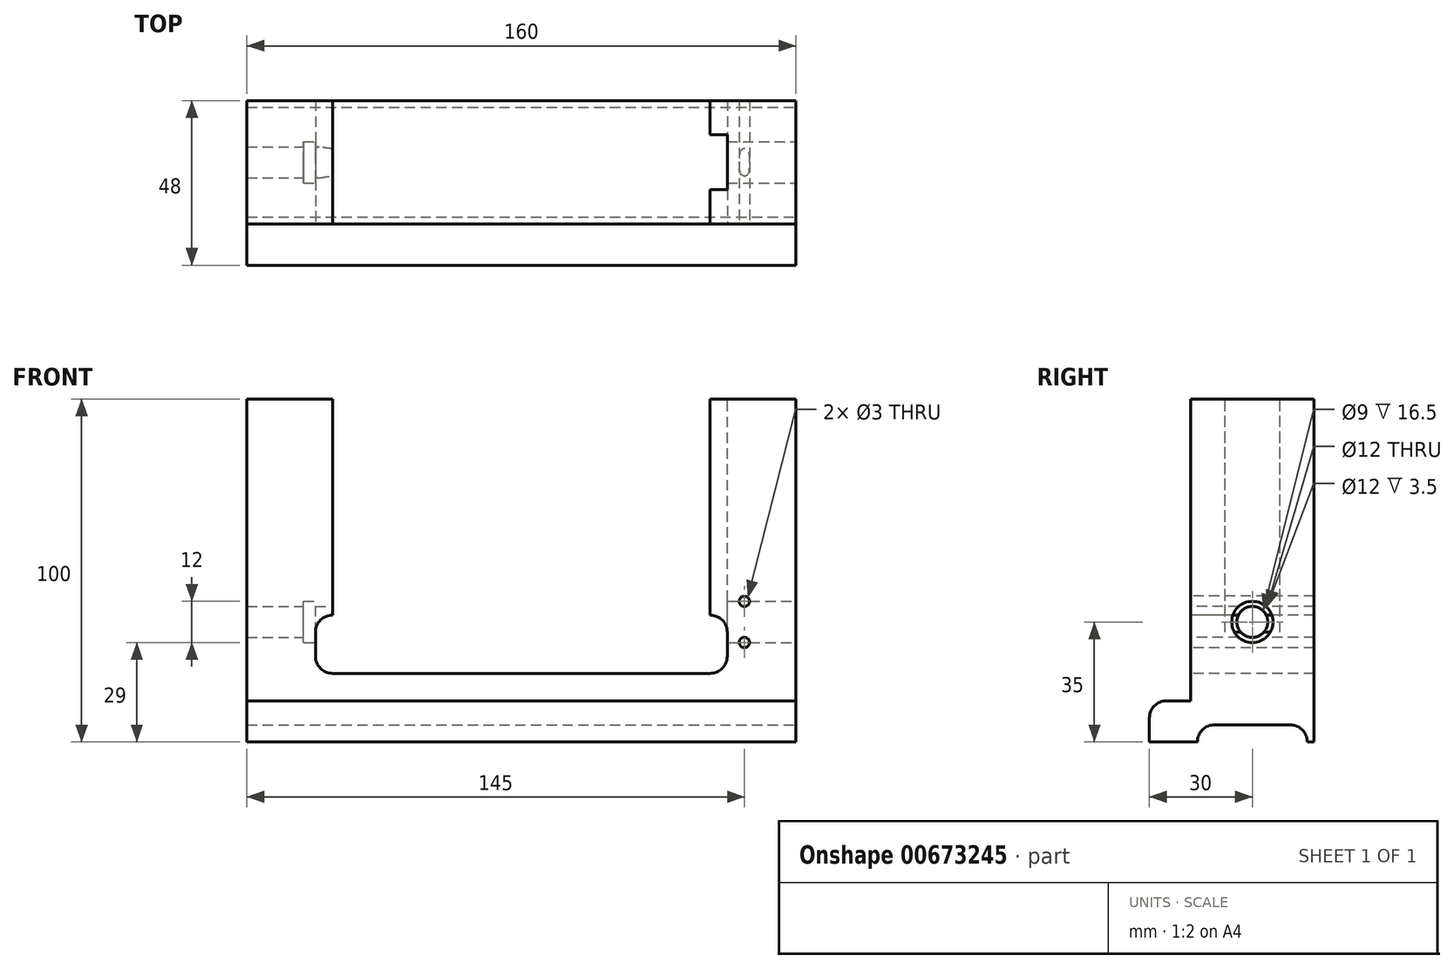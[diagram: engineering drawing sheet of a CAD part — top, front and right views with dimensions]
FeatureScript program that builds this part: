
annotation { "Feature Type Name" : "Feature", "Feature Type Description" : "" }
export const myFeature = defineFeature(function(context is Context, id is Id, definition is map)
    precondition{}
    {
        {
            var Q0;
            Q0=qCreatedBy(makeId("Front.planeOp"),FACE);
            var sketch = newSketch(context, id + "F0", { "sketchPlane" : qUnion([Q0])});
            skLineSegment(sketch, "E0.bottom", {"start": v(-80, 0) * mm, "end": v(80, 0) * mm});
            skLineSegment(sketch, "E0.top", {"start": v(-80, 100) * mm, "end": v(80, 100) * mm});
            skLineSegment(sketch, "E0.left", {"start": v(-80, 0) * mm, "end": v(-80, 100) * mm});
            skLineSegment(sketch, "E0.right", {"start": v(80, 0) * mm, "end": v(80, 100) * mm});
            skSolve(sketch);
        }
        {
            var Q0;
            Q0=makeQuery(id+"F0.imprint","IMPRINT",FACE,{"disambiguationData":[TD([[makeQuery(id+"F0.imprint","IMPRINT",EDGE,{"derivedFrom":sQuery(id+"F0.wireOp",EDGE,"E0.bottom")}),1.0]])]});
            extrude(context, id + "F1", {"entities" : qUnion([Q0]), "depth" : 36 * mm, "offsetDistance" : 25 * mm, "symmetric" : true});
        }
        {
            var Q0;
            Q0=makeQuery(id+"F1.opExtrude","CAP_FACE",FACE,{"disambiguationData":[OSD([sQuery(id+"F0.wireOp",EDGE,"E0.bottom"),sQuery(id+"F0.wireOp",EDGE,"E0.top"),sQuery(id+"F0.wireOp",EDGE,"E0.left"),sQuery(id+"F0.wireOp",EDGE,"E0.right")])],"isStart":false});
            var sketch = newSketch(context, id + "F2", { "sketchPlane" : qUnion([Q0])});
            skLineSegment(sketch, "E1.bottom", {"start": v(-80, 0) * mm, "end": v(80, 0) * mm});
            skLineSegment(sketch, "E1.top", {"start": v(-80, 12) * mm, "end": v(80, 12) * mm});
            skLineSegment(sketch, "E1.left", {"start": v(-80, 0) * mm, "end": v(-80, 12) * mm});
            skLineSegment(sketch, "E1.right", {"start": v(80, 0) * mm, "end": v(80, 12) * mm});
            skSolve(sketch);
        }
        {
            var Q0;
            Q0=makeQuery(id+"F2.imprint","IMPRINT",FACE,{"disambiguationData":[TD([[makeQuery(id+"F2.imprint","IMPRINT",EDGE,{"derivedFrom":sQuery(id+"F2.wireOp",EDGE,"E1.bottom")}),1.0]])]});
            extrude(context, id + "F3", {"entities" : qUnion([Q0]), "operationType" : NewBodyOperationType.ADD, "depth" : 12 * mm, "offsetDistance" : 25 * mm});
        }
        {
            var Q0;
            Q0=makeQuery(id+"F1.opExtrude","CAP_FACE",FACE,{"disambiguationData":[OSD([sQuery(id+"F0.wireOp",EDGE,"E0.bottom"),sQuery(id+"F0.wireOp",EDGE,"E0.top"),sQuery(id+"F0.wireOp",EDGE,"E0.left"),sQuery(id+"F0.wireOp",EDGE,"E0.right")])],"isStart":false});
            var sketch = newSketch(context, id + "F4", { "sketchPlane" : qUnion([Q0])});
            skLineSegment(sketch, "E2.bottom", {"start": v(-55, 100) * mm, "end": v(55, 100) * mm});
            skLineSegment(sketch, "E2.left", {"start": v(-55, 100) * mm, "end": v(-55, 37) * mm});
            skLineSegment(sketch, "E2.right", {"start": v(55, 100) * mm, "end": v(55, 37) * mm});
            skLineSegment(sketch, "E3.bottom", {"start": v(-60, 20) * mm, "end": v(60, 20) * mm});
            skLineSegment(sketch, "E3.top", {"start": v(-60, 37) * mm, "end": v(-55, 37) * mm});
            skLineSegment(sketch, "E3.left", {"start": v(-60, 20) * mm, "end": v(-60, 37) * mm});
            skLineSegment(sketch, "E3.right", {"start": v(60, 20) * mm, "end": v(60, 37) * mm});
            skLineSegment(sketch, "E4.trimOffspring", {"start": v(55, 37) * mm, "end": v(60, 37) * mm});
            skSolve(sketch);
        }
        {
            var Q0;
            Q0=makeQuery(id+"F4.imprint","IMPRINT",FACE,{"disambiguationData":[TD([[makeQuery(id+"F4.imprint","IMPRINT",EDGE,{"derivedFrom":sQuery(id+"F4.wireOp",EDGE,"E2.bottom")}),-1.0]])]});
            extrude(context, id + "F5", {"entities" : qUnion([Q0]), "operationType" : NewBodyOperationType.REMOVE, "endBound" : BoundingType.THROUGH_ALL, "oppositeDirection" : true, "depth" : 25 * mm, "offsetDistance" : 25 * mm});
        }
        {
            var Q0;
            Q0=makeQuery(id+"F3.opExtrude","CAP_EDGE",EDGE,{"disambiguationData":[OSD([sQuery(id+"F2.wireOp",EDGE,"E1.top")])],"isStart":true});
            var Q1;
            Q1=makeQuery(id+"F3.opExtrude","CAP_EDGE",EDGE,{"disambiguationData":[OSD([sQuery(id+"F2.wireOp",EDGE,"E1.top")])],"isStart":false});
            var Q2;
            Q2=makeQuery(id+"FdwUagCk7FOIXWf_1.1.F3.opExtrude","CAP_EDGE",EDGE,{"disambiguationData":[OSD([sQuery(id+"F2.wireOp",EDGE,"E1.top")])],"isStart":true});
            var Q3;
            Q3=makeQuery(id+"FdwUagCk7FOIXWf_1.1.F3.opExtrude","CAP_EDGE",EDGE,{"disambiguationData":[OSD([sQuery(id+"F2.wireOp",EDGE,"E1.top")])],"isStart":false});
            var Q4;
            Q4=makeQuery(id+"F5.boolean.opBoolean","COPY",EDGE,{"derivedFrom":makeQuery(id+"F5.opExtrude","SWEPT_EDGE",EDGE,{"disambiguationData":[OSD([sQuery(id+"F4.wireOp",EDGE,"E3.top"),sQuery(id+"F4.wireOp",EDGE,"E3.left")])]})});
            var Q5;
            Q5=makeQuery(id+"F5.boolean.opBoolean","COPY",EDGE,{"derivedFrom":makeQuery(id+"F5.opExtrude","SWEPT_EDGE",EDGE,{"disambiguationData":[OSD([sQuery(id+"F4.wireOp",EDGE,"E3.bottom"),sQuery(id+"F4.wireOp",EDGE,"E3.left")])]})});
            var Q6;
            Q6=makeQuery(id+"F5.boolean.opBoolean","COPY",EDGE,{"derivedFrom":makeQuery(id+"F5.opExtrude","SWEPT_EDGE",EDGE,{"disambiguationData":[OSD([sQuery(id+"F4.wireOp",EDGE,"E3.bottom"),sQuery(id+"F4.wireOp",EDGE,"E3.right")])]})});
            var Q7;
            Q7=makeQuery(id+"F5.boolean.opBoolean","COPY",EDGE,{"derivedFrom":makeQuery(id+"F5.opExtrude","SWEPT_EDGE",EDGE,{"disambiguationData":[OSD([sQuery(id+"F4.wireOp",EDGE,"E3.right"),sQuery(id+"F4.wireOp",EDGE,"E4.trimOffspring")])]})});
            fillet(context, id + "F6", {"entities" : qUnion([Q0, Q1, Q2, Q3, Q4, Q5, Q6, Q7]), "radius" : 5 * mm, "tangentPropagation" : true, "allowEdgeOverflow" : false});
        }
        {
            var Q0;
            {var subQ0=sQuery(id+"F2.wireOp",EDGE,"E1.right");Q0=makeQuery(id+"FdwUagCk7FOIXWf_1.1.F3.boolean.opBoolean","MERGE",FACE,{"derivedFrom":[makeQuery(id+"F3.boolean.opBoolean","MERGE",FACE,{"derivedFrom":[makeQuery(id+"F1.opExtrude","SWEPT_FACE",FACE,{"disambiguationData":[OSD([sQuery(id+"F0.wireOp",EDGE,"E0.right")])]}),makeQuery(id+"F3.opExtrude","SWEPT_FACE",FACE,{"disambiguationData":[OSD([subQ0])]})]}),makeQuery(id+"FdwUagCk7FOIXWf_1.1.F3.opExtrude","SWEPT_FACE",FACE,{"disambiguationData":[OSD([subQ0])]})]});}
            var sketch = newSketch(context, id + "F7", { "sketchPlane" : qUnion([Q0])});
            skLineSegment(sketch, "E5.bottom", {"start": v(-16, 0) * mm, "end": v(16, 0) * mm});
            skLineSegment(sketch, "E5.top", {"start": v(-16, 5) * mm, "end": v(16, 5) * mm});
            skLineSegment(sketch, "E5.left", {"start": v(-16, 0) * mm, "end": v(-16, 5) * mm});
            skLineSegment(sketch, "E5.right", {"start": v(16, 0) * mm, "end": v(16, 5) * mm});
            skSolve(sketch);
        }
        {
            var Q0;
            Q0=makeQuery(id+"F7.imprint","IMPRINT",FACE,{"disambiguationData":[TD([[makeQuery(id+"F7.imprint","IMPRINT",EDGE,{"derivedFrom":sQuery(id+"F7.wireOp",EDGE,"E5.bottom")}),1.0]])]});
            extrude(context, id + "F8", {"entities" : qUnion([Q0]), "operationType" : NewBodyOperationType.REMOVE, "oppositeDirection" : true, "depth" : 308.5 * mm, "offsetDistance" : 25 * mm});
        }
        {
            var Q0;
            Q0=makeQuery(id+"F8.boolean.opBoolean","COPY",EDGE,{"derivedFrom":makeQuery(id+"F8.opExtrude","SWEPT_EDGE",EDGE,{"disambiguationData":[OSD([sQuery(id+"F7.wireOp",EDGE,"E5.top"),sQuery(id+"F7.wireOp",EDGE,"E5.left")])]})});
            var Q1;
            Q1=makeQuery(id+"F8.boolean.opBoolean","COPY",EDGE,{"derivedFrom":makeQuery(id+"F8.opExtrude","SWEPT_EDGE",EDGE,{"disambiguationData":[OSD([sQuery(id+"F7.wireOp",EDGE,"E5.top"),sQuery(id+"F7.wireOp",EDGE,"E5.right")])]})});
            fillet(context, id + "F9", {"entities" : qUnion([Q0, Q1]), "radius" : 5 * mm, "tangentPropagation" : true, "allowEdgeOverflow" : false});
        }
        {
            var Q0;
            {var subQ1=sQuery(id+"F0.wireOp",EDGE,"E0.right");var subQ3=sQuery(id+"F0.wireOp",EDGE,"E0.top");Q0=makeQuery(id+"F5.boolean.opBoolean","SPLIT",FACE,{"disambiguationData":[TD([makeQuery(id+"F1.opExtrude","SWEPT_FACE",FACE,{"disambiguationData":[OSD([subQ1])]})])],"derivedFrom":makeQuery(id+"F1.opExtrude","SWEPT_FACE",FACE,{"disambiguationData":[OSD([subQ3])]})});}
            var sketch = newSketch(context, id + "F10", { "sketchPlane" : qUnion([Q0])});
            skLineSegment(sketch, "E6.bottom", {"start": v(55, -8) * mm, "end": v(60, -8) * mm});
            skLineSegment(sketch, "E6.top", {"start": v(55, 8) * mm, "end": v(60, 8) * mm});
            skLineSegment(sketch, "E6.left", {"start": v(55, -8) * mm, "end": v(55, 8) * mm});
            skLineSegment(sketch, "E6.right", {"start": v(60, -8) * mm, "end": v(60, 8) * mm});
            skSolve(sketch);
        }
        {
            var Q0;
            Q0 = qSketchRegion(id + "F10", true);
            extrude(context, id + "F11", {"entities" : qUnion([Q0]), "operationType" : NewBodyOperationType.REMOVE, "oppositeDirection" : true, "depth" : 70.3 * mm, "offsetDistance" : 25 * mm});
        }
        {
            var Q0;
            {var subQ0=sQuery(id+"F2.wireOp",EDGE,"E1.right");Q0=makeQuery(id+"FdwUagCk7FOIXWf_1.1.F3.boolean.opBoolean","MERGE",FACE,{"derivedFrom":[makeQuery(id+"F3.boolean.opBoolean","MERGE",FACE,{"derivedFrom":[makeQuery(id+"F1.opExtrude","SWEPT_FACE",FACE,{"disambiguationData":[OSD([sQuery(id+"F0.wireOp",EDGE,"E0.right")])]}),makeQuery(id+"F3.opExtrude","SWEPT_FACE",FACE,{"disambiguationData":[OSD([subQ0])]})]}),makeQuery(id+"FdwUagCk7FOIXWf_1.1.F3.opExtrude","SWEPT_FACE",FACE,{"disambiguationData":[OSD([subQ0])]})]});}
            var sketch = newSketch(context, id + "F12", { "sketchPlane" : qUnion([Q0])});
            skCircle(sketch, "E7", {"center": v(0, 35) * mm, "radius": 4.5 * mm});
            skSolve(sketch);
        }
        {
            var Q0;
            Q0=makeQuery(id+"F12.imprint","IMPRINT",FACE,{"disambiguationData":[TD([[makeQuery(id+"F12.imprint","IMPRINT",EDGE,{"derivedFrom":sQuery(id+"F12.wireOp",EDGE,"E7")}),1.0]])]});
            extrude(context, id + "F13", {"entities" : qUnion([Q0]), "operationType" : NewBodyOperationType.REMOVE, "oppositeDirection" : true, "depth" : 346 * mm, "offsetDistance" : 25 * mm});
        }
        {
            var Q0;
            Q0=makeQuery(id+"F1.opExtrude","CAP_FACE",FACE,{"disambiguationData":[OSD([sQuery(id+"F0.wireOp",EDGE,"E0.bottom"),sQuery(id+"F0.wireOp",EDGE,"E0.top"),sQuery(id+"F0.wireOp",EDGE,"E0.left"),sQuery(id+"F0.wireOp",EDGE,"E0.right")])],"isStart":false});
            var sketch = newSketch(context, id + "F14", { "sketchPlane" : qUnion([Q0])});
            skCircle(sketch, "E8", {"center": v(65, 29) * mm, "radius": 1.5 * mm});
            skCircle(sketch, "E9", {"center": v(65, 41) * mm, "radius": 1.5 * mm});
            skSolve(sketch);
        }
        {
            var Q0;
            {var subQ0=sQuery(id+"F2.wireOp",EDGE,"E1.right");Q0=makeQuery(id+"FdwUagCk7FOIXWf_1.1.F3.boolean.opBoolean","MERGE",FACE,{"derivedFrom":[makeQuery(id+"F3.boolean.opBoolean","MERGE",FACE,{"derivedFrom":[makeQuery(id+"F1.opExtrude","SWEPT_FACE",FACE,{"disambiguationData":[OSD([sQuery(id+"F0.wireOp",EDGE,"E0.right")])]}),makeQuery(id+"F3.opExtrude","SWEPT_FACE",FACE,{"disambiguationData":[OSD([subQ0])]})]}),makeQuery(id+"FdwUagCk7FOIXWf_1.1.F3.opExtrude","SWEPT_FACE",FACE,{"disambiguationData":[OSD([subQ0])]})]});}
            var sketch = newSketch(context, id + "F15", { "sketchPlane" : qUnion([Q0])});
            skCircle(sketch, "E10", {"center": v(0, 35) * mm, "radius": 6 * mm});
            skCircle(sketch, "E11.0", {"center": v(0, 35) * mm, "radius": 4.5 * mm});
            skSolve(sketch);
        }
        {
            var Q0;
            Q0=makeQuery(id+"F15.imprint","IMPRINT",FACE,{"disambiguationData":[TD([[makeQuery(id+"F15.imprint","IMPRINT",EDGE,{"derivedFrom":sQuery(id+"F15.wireOp",EDGE,"E10")}),1.0]])]});
            var Q1;
            Q1=makeQuery(id+"F11.boolean.opBoolean","MERGE",FACE,{"derivedFrom":[makeQuery(id+"F5.boolean.opBoolean","COPY",FACE,{"derivedFrom":makeQuery(id+"F5.opExtrude","SWEPT_FACE",FACE,{"disambiguationData":[OSD([sQuery(id+"F4.wireOp",EDGE,"E3.right")])]})}),makeQuery(id+"F11.opExtrude","SWEPT_FACE",FACE,{"disambiguationData":[OSD([sQuery(id+"F10.wireOp",EDGE,"E6.right")])]})]});
            extrude(context, id + "F16", {"entities" : qUnion([Q0]), "operationType" : NewBodyOperationType.REMOVE, "endBound" : BoundingType.UP_TO_SURFACE, "oppositeDirection" : true, "depth" : 25 * mm, "endBoundEntityFace" : qUnion([Q1]), "offsetDistance" : 25 * mm});
        }
        {
            var Q0;
            Q0=makeQuery(id+"F14.imprint","IMPRINT",FACE,{"disambiguationData":[TD([[makeQuery(id+"F14.imprint","IMPRINT",EDGE,{"derivedFrom":sQuery(id+"F14.wireOp",EDGE,"E9")}),1.0]])]});
            var Q1;
            Q1=makeQuery(id+"F14.imprint","IMPRINT",FACE,{"disambiguationData":[TD([[makeQuery(id+"F14.imprint","IMPRINT",EDGE,{"derivedFrom":sQuery(id+"F14.wireOp",EDGE,"E8")}),1.0]])]});
            extrude(context, id + "F17", {"entities" : qUnion([Q0, Q1]), "operationType" : NewBodyOperationType.REMOVE, "endBound" : BoundingType.THROUGH_ALL, "oppositeDirection" : true, "depth" : 25 * mm, "offsetDistance" : 25 * mm});
        }
        {
            var Q0;
            Q0=makeQuery(id+"FxDg4Hb1j5veAJH_1.1.F11.boolean.opBoolean","MERGE",FACE,{"derivedFrom":[makeQuery(id+"F5.boolean.opBoolean","COPY",FACE,{"derivedFrom":makeQuery(id+"F5.opExtrude","SWEPT_FACE",FACE,{"disambiguationData":[OSD([sQuery(id+"F4.wireOp",EDGE,"E3.left")])]})}),makeQuery(id+"FxDg4Hb1j5veAJH_1.1.F11.opExtrude","SWEPT_FACE",FACE,{"disambiguationData":[OSD([sQuery(id+"F10.wireOp",EDGE,"E6.right")])]})]});
            var sketch = newSketch(context, id + "F18", { "sketchPlane" : qUnion([Q0])});
            skCircle(sketch, "E12", {"center": v(0, 35) * mm, "radius": 6 * mm});
            skSolve(sketch);
        }
        {
            var Q0;
            Q0=makeQuery(id+"F18.imprint","IMPRINT",FACE,{"disambiguationData":[TD([[makeQuery(id+"F18.imprint","IMPRINT",EDGE,{"derivedFrom":sQuery(id+"F18.wireOp",EDGE,"E12")}),1.0]])]});
            extrude(context, id + "F19", {"entities" : qUnion([Q0]), "operationType" : NewBodyOperationType.REMOVE, "oppositeDirection" : true, "depth" : 3.5 * mm, "offsetDistance" : 25 * mm});
        }
    });
